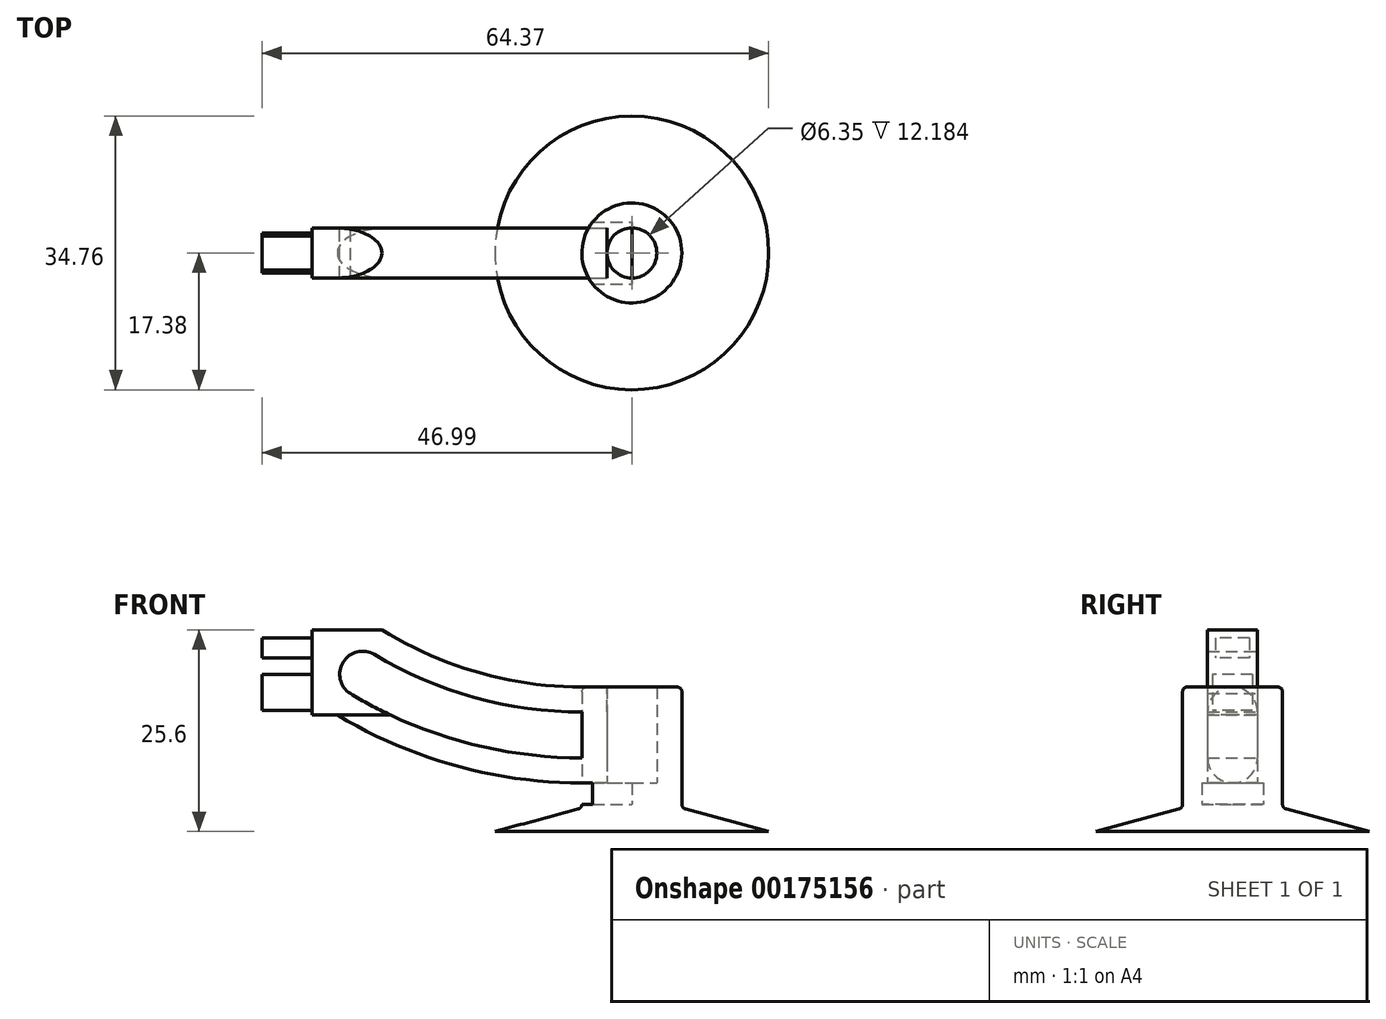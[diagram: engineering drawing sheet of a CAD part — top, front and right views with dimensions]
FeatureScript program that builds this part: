
annotation { "Feature Type Name" : "Feature", "Feature Type Description" : "" }
export const myFeature = defineFeature(function(context is Context, id is Id, definition is map)
    precondition{}
    {
        {
            var Q0;
            Q0=qCreatedBy(makeId("Front.planeOp"),FACE);
            var sketch = newSketch(context, id + "F0", { "sketchPlane" : qUnion([Q0])});
            skLineSegment(sketch, "E0", {"start": v(0, 0) * mm, "end": v(-3.18, 0) * mm});
            skLineSegment(sketch, "E1", {"start": v(0, 0) * mm, "end": v(0, -3.18) * mm});
            skLineSegment(sketch, "E2", {"start": v(-6.35, 12.18) * mm, "end": v(-3.18, 12.18) * mm});
            skLineSegment(sketch, "E3", {"start": v(-3.18, 12.18) * mm, "end": v(-3.18, 0) * mm});
            skLineSegment(sketch, "E4", {"start": v(-6.35, -3.2) * mm, "end": v(-17.38, -6.16) * mm});
            skLineSegment(sketch, "E5", {"start": v(-17.38, -6.16) * mm, "end": v(0, -6.16) * mm});
            skLineSegment(sketch, "E6", {"start": v(0, -6.16) * mm, "end": v(0, -3.18) * mm});
            skArc(sketch, "E7", {"start": v(-31.75, 19.44) * mm, "mid": v(-19.56, 14.03) * mm, "end": v(-6.35, 12.18) * mm});
            skArc(sketch, "E8", {"start": v(-37.4, 8.61) * mm, "mid": v(-22.46, 2.2) * mm, "end": v(-6.35, 0) * mm});
            skLineSegment(sketch, "E9", {"start": v(-31.75, 19.44) * mm, "end": v(-40.64, 19.44) * mm});
            skLineSegment(sketch, "E10", {"start": v(-6.35, 0) * mm, "end": v(-6.35, -3.2) * mm});
            skLineSegment(sketch, "E11", {"start": v(-6.35, 0) * mm, "end": v(-3.18, 0) * mm});
            skArc(sketch, "E12.0", {"start": v(-32.7, 16.3) * mm, "mid": v(-20.02, 10.87) * mm, "end": v(-6.35, 9) * mm});
            skArc(sketch, "E13.0", {"start": v(-35.76, 11.34) * mm, "mid": v(-21.61, 5.25) * mm, "end": v(-6.35, 3.18) * mm});
            skArc(sketch, "E14", {"start": v(-32.7, 16.3) * mm, "mid": v(-36.7, 15.33) * mm, "end": v(-35.76, 11.34) * mm});
            skLineSegment(sketch, "E15", {"start": v(-37.4, 8.61) * mm, "end": v(-40.64, 8.61) * mm});
            skLineSegment(sketch, "E16", {"start": v(-40.64, 19.44) * mm, "end": v(-40.64, 8.61) * mm});
            skLineSegment(sketch, "E17", {"start": v(-6.35, 12.18) * mm, "end": v(-6.35, 0) * mm});
            skLineSegment(sketch, "E18", {"start": v(0, 0) * mm, "end": v(0, 15.56) * mm});
            skLineSegment(sketch, "E19", {"start": v(0, 0) * mm, "end": v(0, -14.58) * mm});
            skPoint(sketch, "E19.endSnap0", {"position": v(0, -1.59) * mm});
            skLineSegment(sketch, "E20", {"start": v(-6.35, 9) * mm, "end": v(-3.18, 9) * mm});
            skLineSegment(sketch, "E21", {"start": v(-6.35, 3.17) * mm, "end": v(-3.18, 3.17) * mm});
            skSolve(sketch);
        }
        {
            var Q0;
            {var subQ2=sQuery(id+"F0.wireOp",EDGE,"E7");Q0=makeQuery(id+"F0.imprint","IMPRINT",FACE,{"disambiguationData":[TD([[makeQuery(id+"F0.imprint","IMPRINT",EDGE,{"derivedFrom":subQ2}),-1.0]])]});}
            var Q1;
            {var subQ0=sQuery(id+"F0.wireOp",EDGE,"E2");Q1=makeQuery(id+"F0.imprint","IMPRINT",FACE,{"disambiguationData":[TD([[makeQuery(id+"F0.imprint","IMPRINT",EDGE,{"derivedFrom":subQ0}),-1.0]])]});}
            var Q2;
            {var subQ0=sQuery(id+"F0.wireOp",EDGE,"E11");Q2=makeQuery(id+"F0.imprint","IMPRINT",FACE,{"disambiguationData":[TD([[makeQuery(id+"F0.imprint","IMPRINT",EDGE,{"derivedFrom":subQ0}),1.0]])]});}
            var Q3;
            {var subQ0=sQuery(id+"F0.wireOp",EDGE,"E20");Q3=makeQuery(id+"F0.imprint","IMPRINT",FACE,{"disambiguationData":[TD([[makeQuery(id+"F0.imprint","IMPRINT",EDGE,{"derivedFrom":subQ0}),-1.0]])]});}
            extrude(context, id + "F1", {"entities" : qUnion([Q0, Q1, Q2, Q3]), "endBound" : BoundingType.SYMMETRIC, "depth" : 6.35 * mm});
        }
        {
            var Q0;
            {var subQ2=sQuery(id+"F0.wireOp",EDGE,"E2");Q0=makeQuery(id+"F0.imprint","IMPRINT",FACE,{"disambiguationData":[TD([[makeQuery(id+"F0.imprint","IMPRINT",EDGE,{"derivedFrom":subQ2}),-1.0]])]});}
            var Q1;
            {var subQ0=sQuery(id+"F0.wireOp",EDGE,"E20");Q1=makeQuery(id+"F0.imprint","IMPRINT",FACE,{"disambiguationData":[TD([[makeQuery(id+"F0.imprint","IMPRINT",EDGE,{"derivedFrom":subQ0}),-1.0]])]});}
            var Q2;
            {var subQ0=sQuery(id+"F0.wireOp",EDGE,"E11");Q2=makeQuery(id+"F0.imprint","IMPRINT",FACE,{"disambiguationData":[TD([[makeQuery(id+"F0.imprint","IMPRINT",EDGE,{"derivedFrom":subQ0}),1.0]])]});}
            var Q3;
            {var subQ1=sQuery(id+"F0.wireOp",EDGE,"E0");Q3=makeQuery(id+"F0.imprint","IMPRINT",FACE,{"disambiguationData":[TD([[makeQuery(id+"F0.imprint","IMPRINT",EDGE,{"derivedFrom":subQ1}),1.0]])]});}
            var Q4;
            Q4=sQuery(id+"F0.wireOp",EDGE,"E18");
            revolve(context, id + "F2", {"entities" : qUnion([Q0, Q1, Q2, Q3]), "axis" : qUnion([Q4]), "revolveType" : RevolveType.FULL});
        }
        {
            var Q0;
            Q0=qCreatedBy(makeId("Right.planeOp"),FACE);
            var sketch = newSketch(context, id + "F3", { "sketchPlane" : qUnion([Q0])});
            skLineSegment(sketch, "E22.bottom", {"start": v(0, 0) * mm, "end": v(3.92, 0) * mm});
            skLineSegment(sketch, "E22.top", {"start": v(0, -2.73) * mm, "end": v(3.92, -2.73) * mm});
            skLineSegment(sketch, "E22.right", {"start": v(3.92, 0) * mm, "end": v(3.92, -2.73) * mm});
            skLineSegment(sketch, "E23.MirrorCS", {"start": v(0, 0) * mm, "end": v(-3.92, 0) * mm});
            skLineSegment(sketch, "E24.MirrorCS", {"start": v(-3.92, 0) * mm, "end": v(-3.92, -2.73) * mm});
            skLineSegment(sketch, "E25.MirrorCS", {"start": v(0, -2.73) * mm, "end": v(-3.92, -2.73) * mm});
            skSolve(sketch);
        }
        {
            var Q0;
            Q0 = qSketchRegion(id + "F3", true);
            extrude(context, id + "F4", {"entities" : qUnion([Q0]), "operationType" : NewBodyOperationType.REMOVE, "oppositeDirection" : true, "depth" : 6.35 * mm});
        }
        {
            var Q0;
            Q0=makeQuery(id+"F1.opExtrude","SWEPT_FACE",FACE,{"disambiguationData":[OSD([sQuery(id+"F0.wireOp",EDGE,"E16")])]});
            var sketch = newSketch(context, id + "F5", { "sketchPlane" : qUnion([Q0])});
            skLineSegment(sketch, "E26.bottom", {"start": v(-2.41, 15.6) * mm, "end": v(2.41, 15.6) * mm});
            skLineSegment(sketch, "E26.top", {"start": v(-2.41, 18.65) * mm, "end": v(2.41, 18.65) * mm});
            skLineSegment(sketch, "E26.left", {"start": v(-2.41, 15.6) * mm, "end": v(-2.41, 18.65) * mm});
            skLineSegment(sketch, "E26.right", {"start": v(2.41, 15.6) * mm, "end": v(2.41, 18.65) * mm});
            skPoint(sketch, "E26.middle", {"position": v(0, 17.13) * mm});
            skLineSegment(sketch, "E27.bottom", {"start": v(-2.8, 14.05) * mm, "end": v(2.8, 14.05) * mm});
            skLineSegment(sketch, "E27.top", {"start": v(-2.8, 8.97) * mm, "end": v(2.8, 8.97) * mm});
            skLineSegment(sketch, "E27.left", {"start": v(-2.8, 14.05) * mm, "end": v(-2.8, 8.97) * mm});
            skLineSegment(sketch, "E27.right", {"start": v(2.8, 14.05) * mm, "end": v(2.8, 8.97) * mm});
            skPoint(sketch, "E27.middle", {"position": v(0, 11.5) * mm});
            skLineSegment(sketch, "E28.bottom", {"start": v(-2.54, 13.8) * mm, "end": v(2.54, 13.8) * mm});
            skLineSegment(sketch, "E28.top", {"start": v(-2.54, 9.22) * mm, "end": v(2.54, 9.22) * mm});
            skLineSegment(sketch, "E28.left", {"start": v(-2.54, 13.8) * mm, "end": v(-2.54, 9.22) * mm});
            skLineSegment(sketch, "E28.right", {"start": v(2.54, 13.8) * mm, "end": v(2.54, 9.22) * mm});
            skLineSegment(sketch, "E29.bottom", {"start": v(-2.16, 18.4) * mm, "end": v(2.16, 18.4) * mm});
            skLineSegment(sketch, "E29.top", {"start": v(-2.16, 15.86) * mm, "end": v(2.16, 15.86) * mm});
            skLineSegment(sketch, "E29.left", {"start": v(-2.16, 18.4) * mm, "end": v(-2.16, 15.86) * mm});
            skLineSegment(sketch, "E29.right", {"start": v(2.16, 18.4) * mm, "end": v(2.16, 15.86) * mm});
            skSolve(sketch);
        }
        {
            var Q0;
            Q0=makeQuery(id+"F5.imprint","IMPRINT",FACE,{"disambiguationData":[TD([[makeQuery(id+"F5.imprint","IMPRINT",EDGE,{"derivedFrom":sQuery(id+"F5.wireOp",EDGE,"E29.bottom")}),-1.0]])]});
            var Q1;
            Q1=makeQuery(id+"F5.imprint","IMPRINT",FACE,{"disambiguationData":[TD([[makeQuery(id+"F5.imprint","IMPRINT",EDGE,{"derivedFrom":sQuery(id+"F5.wireOp",EDGE,"E28.bottom")}),-1.0]])]});
            extrude(context, id + "F6", {"entities" : qUnion([Q0, Q1]), "operationType" : NewBodyOperationType.ADD, "depth" : 6.35 * mm});
        }
        {
            var Q0;
            Q0=makeQuery(id+"F2.opRevolve","SWEPT_EDGE",EDGE,{"disambiguationData":[OSD([sQuery(id+"F0.wireOp",EDGE,"E2"),sQuery(id+"F0.wireOp",EDGE,"E7"),sQuery(id+"F0.wireOp",EDGE,"E17")])]});
            var Q1;
            Q1=makeQuery(id+"F2.opRevolve","SWEPT_EDGE",EDGE,{"disambiguationData":[OSD([sQuery(id+"F0.wireOp",EDGE,"E4"),sQuery(id+"F0.wireOp",EDGE,"E10")])]});
            fillet(context, id + "F7", {"entities" : qUnion([Q0, Q1]), "radius" : 0.64 * mm, "tangentPropagation" : true, "allowEdgeOverflow" : false});
        }
        {
            var Q0;
            Q0=makeQuery(id+"F1.opExtrude","CAP_EDGE",EDGE,{"disambiguationData":[OSD([sQuery(id+"F0.wireOp",EDGE,"E7")])],"isStart":false});
            var Q1;
            Q1=makeQuery(id+"F1.opExtrude","CAP_EDGE",EDGE,{"disambiguationData":[OSD([sQuery(id+"F0.wireOp",EDGE,"E7")])],"isStart":true});
            var Q2;
            Q2=makeQuery(id+"F1.opExtrude","CAP_EDGE",EDGE,{"disambiguationData":[OSD([sQuery(id+"F0.wireOp",EDGE,"E8")])],"isStart":false});
            var Q3;
            Q3=makeQuery(id+"F1.opExtrude","CAP_EDGE",EDGE,{"disambiguationData":[OSD([sQuery(id+"F0.wireOp",EDGE,"E8")])],"isStart":true});
            fillet(context, id + "F8", {"entities" : qUnion([Q0, Q1, Q2, Q3]), "radius" : 3.17 * mm, "tangentPropagation" : true, "allowEdgeOverflow" : false});
        }
    });
